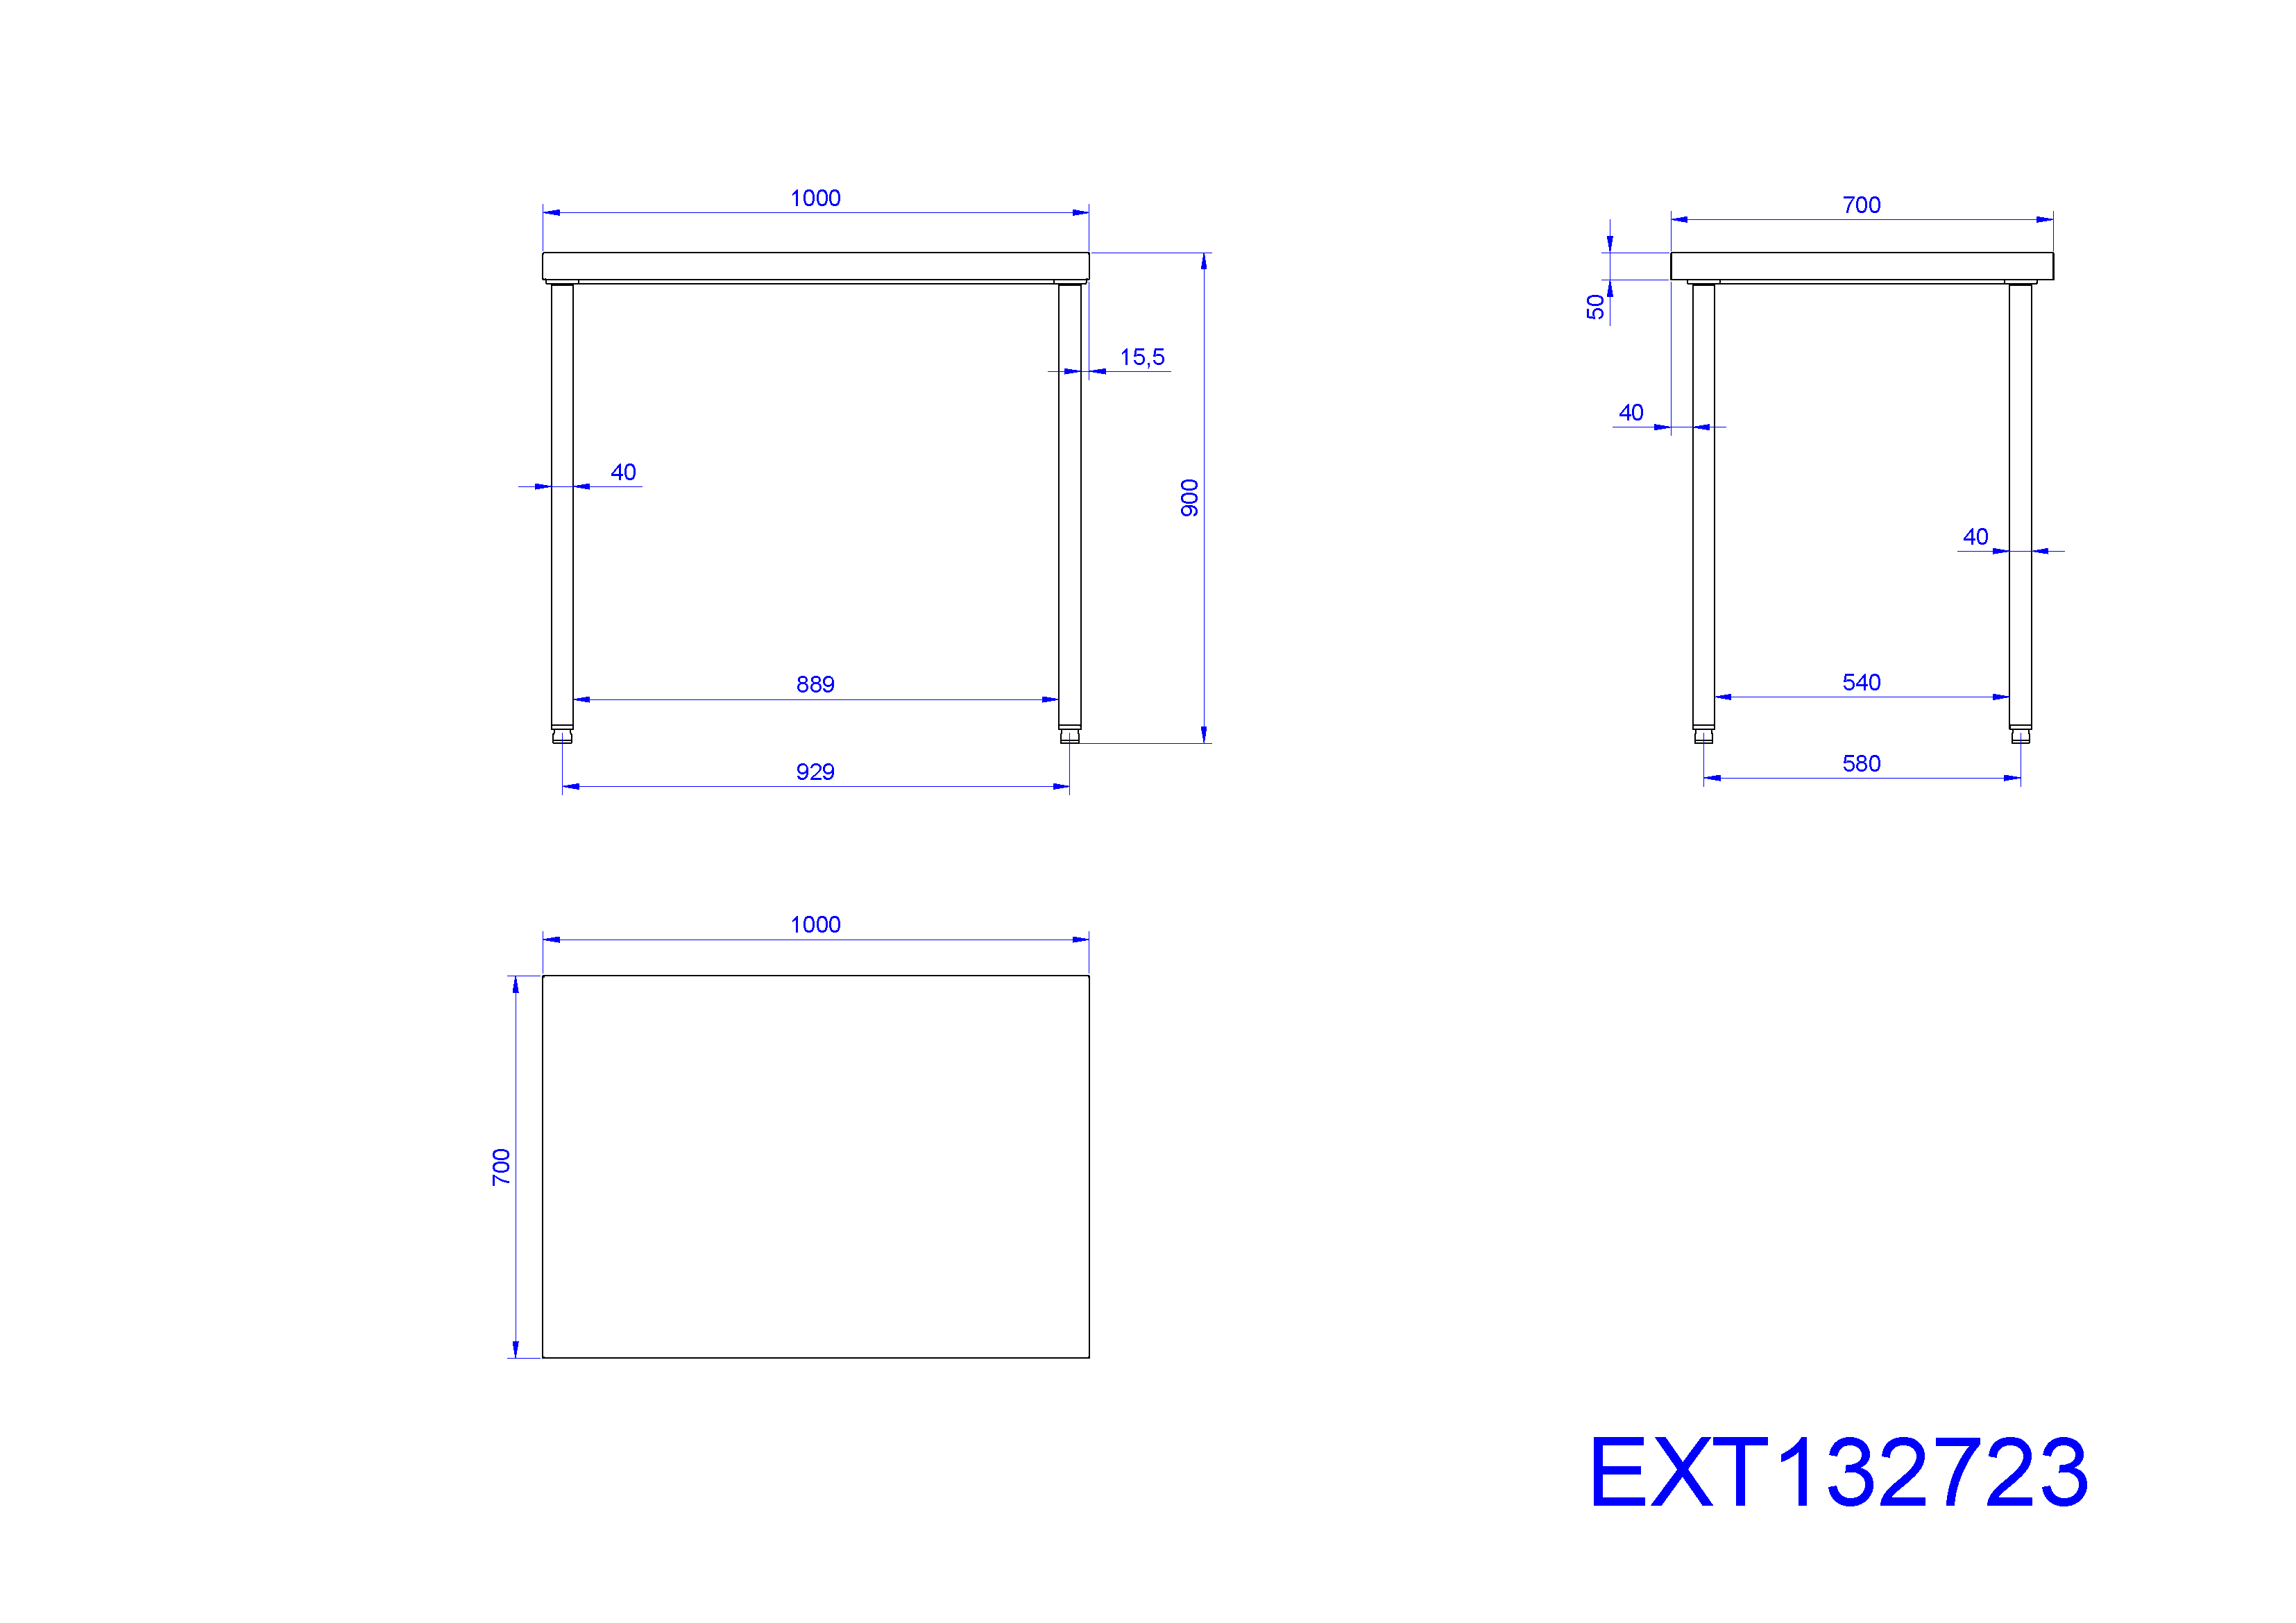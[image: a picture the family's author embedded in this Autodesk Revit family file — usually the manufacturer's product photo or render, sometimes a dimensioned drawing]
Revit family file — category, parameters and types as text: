
# Revit family: QF_ZANUSSI_132842_WTD1607N
name_source: partatom
category: Attrezzature speciali
units: mm (PartAtom-declared; Revit-internal decimal feet)

## family parameters
Basato su piano di lavoro = No
Condiviso = No
Punto di calcolo locali = No
Quota connettore circolare = Usa diametro
Sempre verticale = Sì
Taglio con vuoti quando caricato = No
Tipo di parte = Normale

## types (1)
- Standard
    Accessory = Sì
    Cold Water Size = 0 mm
    Compressed Air Pressure = 0.0 Pa
    Compressed Air Size = 0 mm
    Compressed Air Volume = 0.0 L/s
    Condensate Return Size = 0 mm
    Cycle = 0 Hz
    Depth Actual = 700 mm  [stored 2.29659 ft]
    Descrizione = WORK TABLE-DISASSEMBLED 1600MM
    Direct Waste Size = 0 mm
    Gas Input Pressure = 0
    Gas KW = 0
    Gas Size = 0 mm
    HP = 0 HP
    Height Actual = 900 mm  [stored 2.95276 ft]
    Hot Water Size = 0 mm
    Item Number = 132842
    Length Actual = 1600 mm  [stored 5.24934 ft]
    Modello = WTD1607N
    Phase = 0
    Produttore = Zanussi
    Prospetto di default = 0 mm  [stored 0 ft]
    Refrigerant Compressor Remote = Sì
    Refrigeration Liquid Line Size = 0 mm  [stored 0 ft]
    Refrigeration Suction Line Size = 0 mm  [stored 0 ft]
    Steam Consumption per Hour = 0
    Steam Supply Maximum Pressure = 0.0 Pa
    Steam Supply Minimum Pressure = 0.0 Pa
    Steam Supply Size = 0 mm
    URL = http://www.zanussiprofessional.com
    URL Manufacturer = http://www.zanussiprofessional.com
    Volts = 0 V
    Watts = 0 W
    Weight = 53.00 kg

note: source unit labels omitted for Gas Input Pressure — the stored unit's dimension contradicts the parameter name (converter mislabeling)

note: [stored X ft] marks values corroborated as IEEE doubles in the binary element streams (Revit-internal decimal feet)

## geometry (parser evidence)
native form markers: Sweep x2
no freeform markers — native parametric forms only
